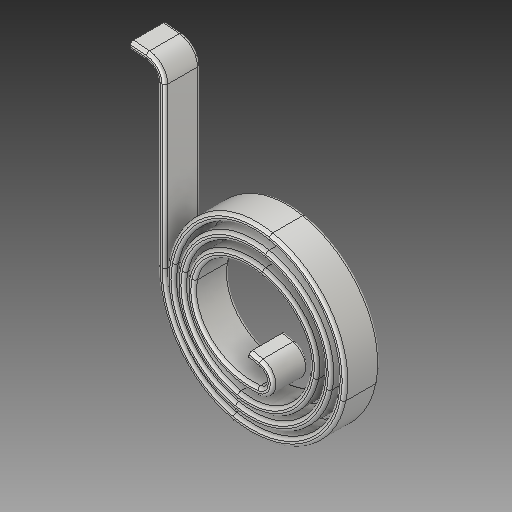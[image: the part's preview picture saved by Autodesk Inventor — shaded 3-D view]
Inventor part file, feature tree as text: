
AUTODESK INVENTOR PART (.ipt)
format: ipt  version: 2019 (Build 230136000, 136)  size: 880,128 bytes
history: native  units: in
note: dims shown in document units (in); Inventor stores cm internally (conversion verified against a paired STEP export)
features: other x3, sketch x1
ambient origin geometry x8: Origin, YZ Plane, XZ Plane, XY Plane, X Axis, Y Axis, Z Axis, Center Point
bodies: Solid1 (feature_tree)
feature tree (4):
  other  "Rear Tilt Spring.ipt"
  other  "Solid1::Rear Tilt Spring.ipt"
  other  "TaggingFeature1"
  sketch  "Sketch1"  dims[d0=0.3937in]
